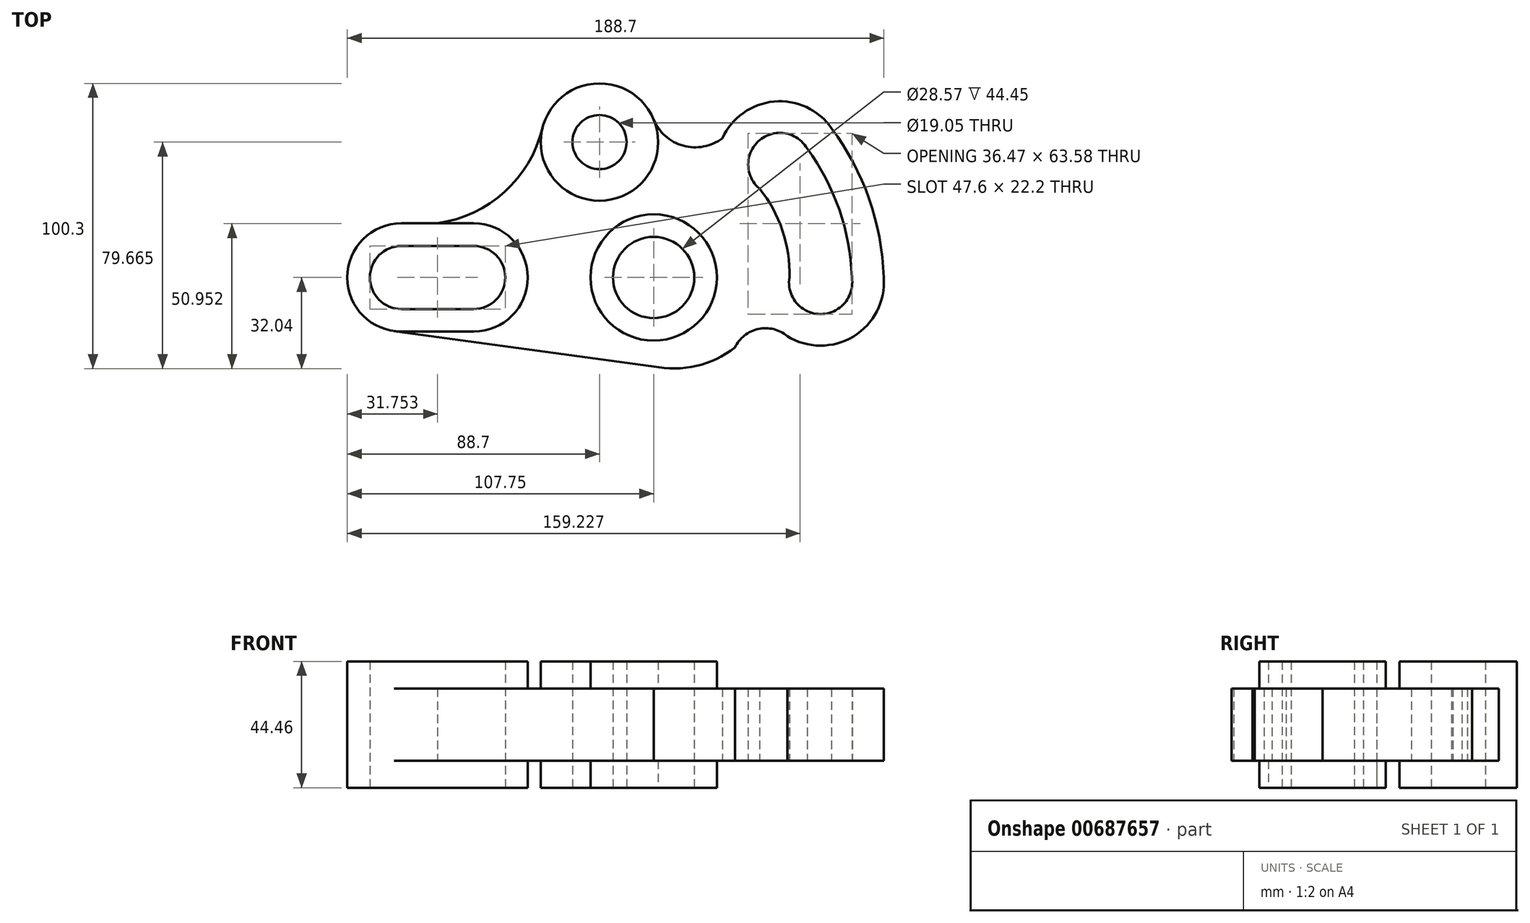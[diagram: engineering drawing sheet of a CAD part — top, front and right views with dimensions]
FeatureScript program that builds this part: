
annotation { "Feature Type Name" : "Feature", "Feature Type Description" : "" }
export const myFeature = defineFeature(function(context is Context, id is Id, definition is map)
    precondition{}
    {
        {
            var Q0;
            Q0=qCreatedBy(makeId("Top.planeOp"),FACE);
            var sketch = newSketch(context, id + "F0", { "sketchPlane" : qUnion([Q0])});
            skCircle(sketch, "E0", {"center": v(0, 0) * mm, "radius": 14.29 * mm});
            skCircle(sketch, "E1", {"center": v(0, 0) * mm, "radius": 22.23 * mm});
            skCircle(sketch, "E2", {"center": v(-19.05, 47.63) * mm, "radius": 9.53 * mm});
            skCircle(sketch, "E3", {"center": v(-19.05, 47.63) * mm, "radius": 20.64 * mm});
            skLineSegment(sketch, "E4", {"start": v(-190.71, 0) * mm, "end": v(180.72, 0) * mm, "construction": true});
            skArc(sketch, "E5", {"start": v(0, 55.56) * mm, "mid": v(10.45, 46.36) * mm, "end": v(24.13, 48.93) * mm});
            skArc(sketch, "E6", {"start": v(47.74, 0) * mm, "mid": v(58.72, -12.88) * mm, "end": v(69.71, 0) * mm});
            skLineSegment(sketch, "E7", {"start": v(0, 0) * mm, "end": v(157.14, 131.86) * mm, "construction": true});
            skArc(sketch, "E8", {"start": v(47.74, 0) * mm, "mid": v(45.3, 16.57) * mm, "end": v(37.21, 31.23) * mm});
            skArc(sketch, "E9", {"start": v(69.71, 0) * mm, "mid": v(65.28, 23.84) * mm, "end": v(54, 45.31) * mm});
            skArc(sketch, "E10", {"start": v(54, 45.31) * mm, "mid": v(37.22, 48.27) * mm, "end": v(37.21, 31.23) * mm});
            skArc(sketch, "E11", {"start": v(-88.7, 11.1) * mm, "mid": v(-99.8, 0) * mm, "end": v(-88.7, -11.1) * mm});
            skLineSegment(sketch, "E12", {"start": v(-88.7, 11.1) * mm, "end": v(-63.3, 11.1) * mm});
            skLineSegment(sketch, "E13", {"start": v(-88.7, -11.1) * mm, "end": v(-63.3, -11.1) * mm});
            skArc(sketch, "E14", {"start": v(-63.3, -11.1) * mm, "mid": v(-52.2, 0) * mm, "end": v(-63.3, 11.1) * mm});
            skArc(sketch, "E15", {"start": v(-88.7, 19.05) * mm, "mid": v(-107.75, 0) * mm, "end": v(-88.7, -19.05) * mm});
            skLineSegment(sketch, "E16", {"start": v(-88.7, 19.05) * mm, "end": v(-63.3, 19.05) * mm});
            skLineSegment(sketch, "E17", {"start": v(-88.7, -19.05) * mm, "end": v(-63.3, -19.05) * mm});
            skArc(sketch, "E18", {"start": v(-63.3, -19.05) * mm, "mid": v(-44.25, 0) * mm, "end": v(-63.3, 19.05) * mm});
            skArc(sketch, "E19", {"start": v(-76, 19.05) * mm, "mid": v(-52.42, 30.13) * mm, "end": v(-39.1, 52.52) * mm});
            skArc(sketch, "E20", {"start": v(62.57, 52.5) * mm, "mid": v(42.31, 61.87) * mm, "end": v(24.13, 48.93) * mm});
            skArc(sketch, "E21", {"start": v(80.88, 0) * mm, "mid": v(75.77, 27.66) * mm, "end": v(62.57, 52.5) * mm});
            skArc(sketch, "E22", {"start": v(46.98, -20.62) * mm, "mid": v(70.27, -20.74) * mm, "end": v(80.88, 0) * mm});
            skLineSegment(sketch, "E23", {"start": v(0, -31.31) * mm, "end": v(-91.27, -18.88) * mm});
            skArc(sketch, "E24", {"start": v(0, -31.31) * mm, "mid": v(15.04, -31.13) * mm, "end": v(28.6, -24.65) * mm});
            skArc(sketch, "E25", {"start": v(46.98, -20.62) * mm, "mid": v(36.8, -18.13) * mm, "end": v(28.6, -24.65) * mm});
            skSolve(sketch);
        }
        {
            var Q0;
            Q0=makeQuery(id+"F0.imprint","IMPRINT",FACE,{"disambiguationData":[TD([[makeQuery(id+"F0.imprint","IMPRINT",EDGE,{"derivedFrom":sQuery(id+"F0.wireOp",EDGE,"E1")}),-1.0]])]});
            extrude(context, id + "F1", {"entities" : qUnion([Q0]), "endBound" : BoundingType.SYMMETRIC, "depth" : 25.4 * mm, "offsetDistance" : 25.4 * mm});
        }
        {
            var Q0;
            Q0=makeQuery(id+"F0.imprint","IMPRINT",FACE,{"disambiguationData":[TD([[makeQuery(id+"F0.imprint","IMPRINT",EDGE,{"derivedFrom":sQuery(id+"F0.wireOp",EDGE,"E11")}),-1.0]])]});
            var Q1;
            Q1=makeQuery(id+"F0.imprint","IMPRINT",FACE,{"disambiguationData":[TD([[makeQuery(id+"F0.imprint","IMPRINT",EDGE,{"derivedFrom":sQuery(id+"F0.wireOp",EDGE,"E2")}),-1.0]])]});
            var Q2;
            Q2=makeQuery(id+"F0.imprint","IMPRINT",FACE,{"disambiguationData":[TD([[makeQuery(id+"F0.imprint","IMPRINT",EDGE,{"derivedFrom":sQuery(id+"F0.wireOp",EDGE,"E0")}),-1.0]])]});
            extrude(context, id + "F2", {"entities" : qUnion([Q0, Q1, Q2]), "operationType" : NewBodyOperationType.ADD, "endBound" : BoundingType.SYMMETRIC, "depth" : 44.45 * mm, "offsetDistance" : 25.4 * mm});
        }
    });
